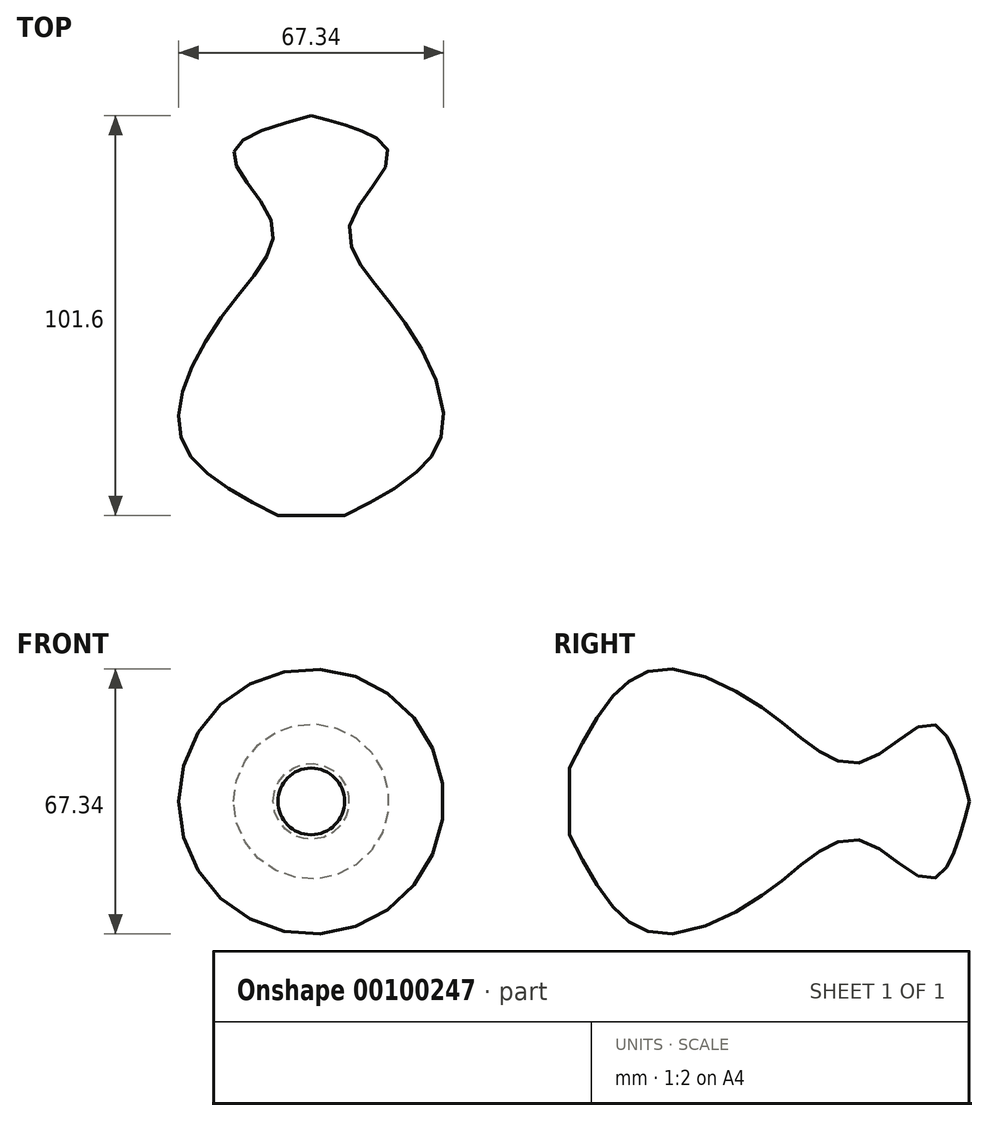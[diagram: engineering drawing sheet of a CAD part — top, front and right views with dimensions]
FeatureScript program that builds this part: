
annotation { "Feature Type Name" : "Feature", "Feature Type Description" : "" }
export const myFeature = defineFeature(function(context is Context, id is Id, definition is map)
    precondition{}
    {
        {
            var Q0;
            Q0=qCreatedBy(makeId("Top.planeOp"),FACE);
            var sketch = newSketch(context, id + "F0", { "sketchPlane" : qUnion([Q0])});
            skFitSpline(sketch, "E0", {"points": [v(-8.47, -25.6) * mm, v(-33.08, -5.56) * mm, v(-21.83, 26.08) * mm, v(-9.87, 48.23) * mm, v(-19.72, 66.16) * mm, v(0, 76) * mm], "startDerivative": vector(-150.13, 75.85) * mm, "endDerivative": vector(152.12, 42.93) * mm});
            skLineSegment(sketch, "E1", {"start": v(-8.47, -25.6) * mm, "end": v(0, -25.6) * mm});
            skLineSegment(sketch, "E2", {"start": v(0, -25.6) * mm, "end": v(0, 76) * mm});
            skSolve(sketch);
        }
        {
            var Q0;
            Q0=makeQuery(id+"F0.imprint","IMPRINT",FACE,{"disambiguationData":[TD([[makeQuery(id+"F0.imprint","IMPRINT",EDGE,{"derivedFrom":sQuery(id+"F0.wireOp",EDGE,"E0")}),-1.0]])]});
            var Q1;
            Q1=sQuery(id+"F0.wireOp",EDGE,"E2");
            revolve(context, id + "F1", {"surfaceOperationType" : NewSurfaceOperationType.NEW, "entities" : qUnion([Q0]), "axis" : qUnion([Q1]), "revolveType" : RevolveType.FULL});
        }
    });
